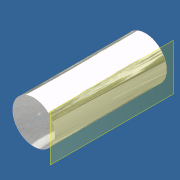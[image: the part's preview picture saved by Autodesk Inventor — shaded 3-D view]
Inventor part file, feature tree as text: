
AUTODESK INVENTOR PART (.ipt)
format: ipt  version: unknown  size: 161,792 bytes
history: native  units: in
note: dims shown in document units (in); Inventor stores cm internally (conversion verified against a paired STEP export)
features: sketch x2, extrude x1, plane x1
ambient origin geometry x8: Origin, YZ Plane, XZ Plane, XY Plane, X Axis, Y Axis, Z Axis, Center Point
bodies: Solid1 (feature_tree)
feature tree (4):
  extrude  "Extrusion1"  Depth=5.502in TaperAngle=0.0deg
  plane  "Work Plane1"
  sketch  "Sketch2"  dims[d3=1.5in]
  sketch  "Sketch1"  dims[d0=2.08in d1=5.502in d2=0.0in]
